# Revit family: Sanitary_Taps-Mixers_AXOR_12408SGP-AXOR-Starck-Single-lever-bath-m_new
name_source: partatom
category: Plumbing Fixtures
revit_build: Autodesk Revit 2018 (Build: 20170223_1515(x64)
units: mm (PartAtom-declared; Revit-internal decimal feet)

## family parameters
Cut with Voids When Loaded = Yes
Host = Face
OmniClass Number = 23.31.11.00
OmniClass Title = Faucets
Part Type = Normal
Room Calculation Point = No
Round Connector Dimension = Use Diameter
Shared = No

## types (1)
- 679 Matte Black
    Always visible = Yes
    BIMobject category = Taps & Mixers
    Default Elevation = 1219 mm
    Description = AXOR Starck Single lever bath mixer floor-standing with flat lever handle 2 ticks
    Design country = Germany
    EAN code = 4059625277003
    Edition number = 1
    IFC Classification = Valve
    Manufacturer = AXOR
    Manufacturer country = Germany
    Manufacturer name = AXOR
    Masterformat 2014 Code = 22 41 39
    Masterformat 2014 Description = Residential Faucets, Supplies, and Trim
    Material = AXOR - Metal - 679 Matte Black
    Model = 12408SGP
    OmniClass Code = 23-31 11 00
    OmniClass Description = Faucets
    Product Guid = 4abe286c-68cd-42d6-bd9c-6bc46977e7d1
    Product SKU = 12408SGP
    Product data url = https://bimobject.com
    Product family = AXOR Starck
    Product group = Bath mixers
    Product name = AXOR Starck Single lever bath mixer floor-standing with flat lever handle 2 ticks
    Product url = https://www.axor-design.com
    QR code = https://bimobject.com
    UNSPSC Code = 301815
    URL = https://www.axor-design.com
    Uniclass 2015 Code = Pr_40_20_87
    Uniclass 2015 Name = Taps and water supply outlet fittings
    Uniformat II Code = D2010
    Uniformat II Description = Plumbing Fixtures
    Version = 1
    Weight Net (Kg) = 8

## geometry (parser evidence)
native form markers: Sweep x2
no freeform markers — native parametric forms only
